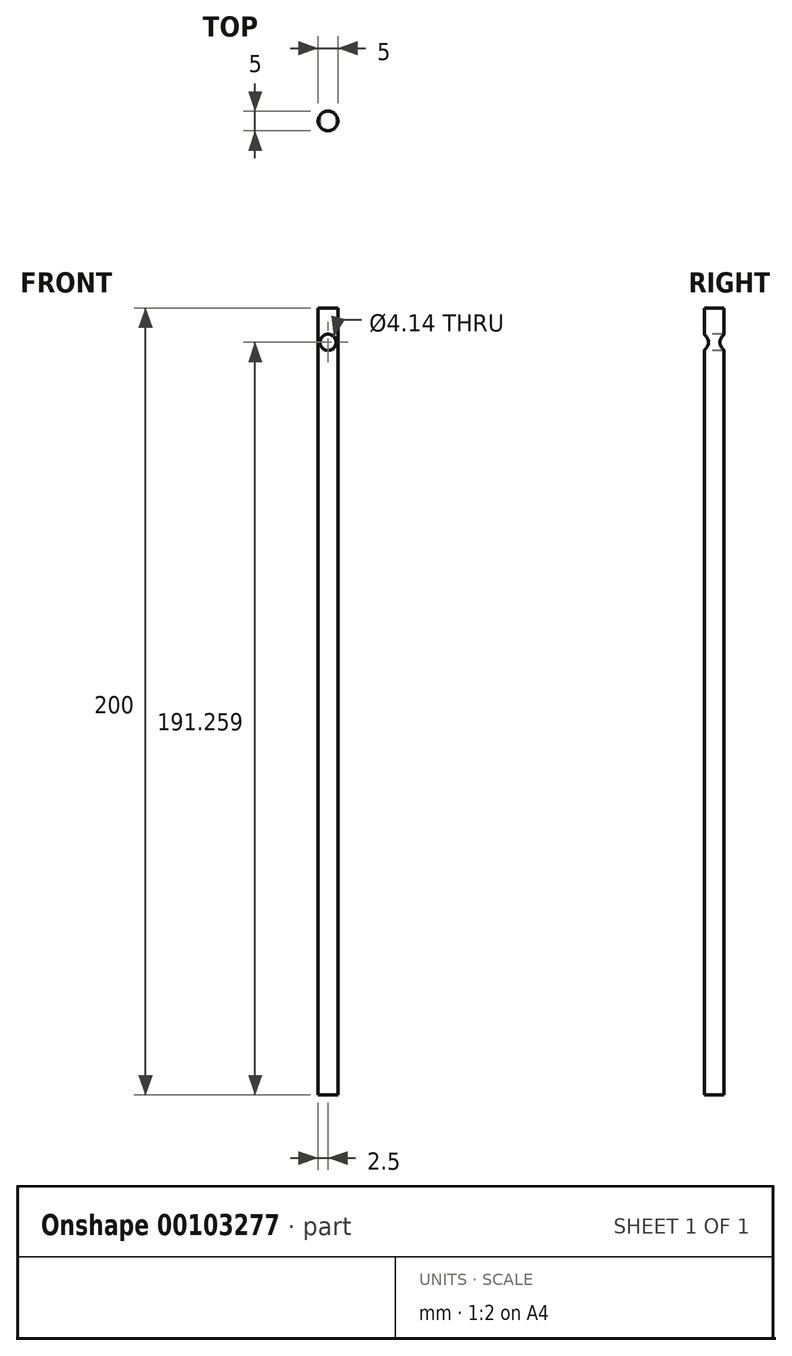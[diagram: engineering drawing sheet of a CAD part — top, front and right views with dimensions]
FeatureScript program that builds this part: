
annotation { "Feature Type Name" : "Feature", "Feature Type Description" : "" }
export const myFeature = defineFeature(function(context is Context, id is Id, definition is map)
    precondition{}
    {
        {
            var Q0;
            Q0=qCreatedBy(makeId("Top.planeOp"),FACE);
            var sketch = newSketch(context, id + "F0", { "sketchPlane" : qUnion([Q0])});
            skCircle(sketch, "E0", {"center": v(0, 0) * mm, "radius": 2.5 * mm});
            skSolve(sketch);
        }
        {
            var Q0;
            Q0=makeQuery(id+"F0.imprint","IMPRINT",FACE,{"disambiguationData":[TD([[makeQuery(id+"F0.imprint","IMPRINT",EDGE,{"derivedFrom":sQuery(id+"F0.wireOp",EDGE,"E0")}),1.0]])]});
            extrude(context, id + "F1", {"entities" : qUnion([Q0]), "endBound" : BoundingType.SYMMETRIC, "depth" : 200 * mm});
        }
        {
            var Q0;
            Q0=qCreatedBy(makeId("Front.planeOp"),FACE);
            var sketch = newSketch(context, id + "F2", { "sketchPlane" : qUnion([Q0])});
            skCircle(sketch, "E1", {"center": v(0, 91.26) * mm, "radius": 2.07 * mm});
            skSolve(sketch);
        }
        {
            var Q0;
            Q0=makeQuery(id+"F2.imprint","IMPRINT",FACE,{"disambiguationData":[TD([[makeQuery(id+"F2.imprint","IMPRINT",EDGE,{"derivedFrom":sQuery(id+"F2.wireOp",EDGE,"E1")}),1.0]])]});
            extrude(context, id + "F3", {"entities" : qUnion([Q0]), "operationType" : NewBodyOperationType.REMOVE, "endBound" : BoundingType.SYMMETRIC, "oppositeDirection" : true, "depth" : 25.4 * mm});
        }
    });
